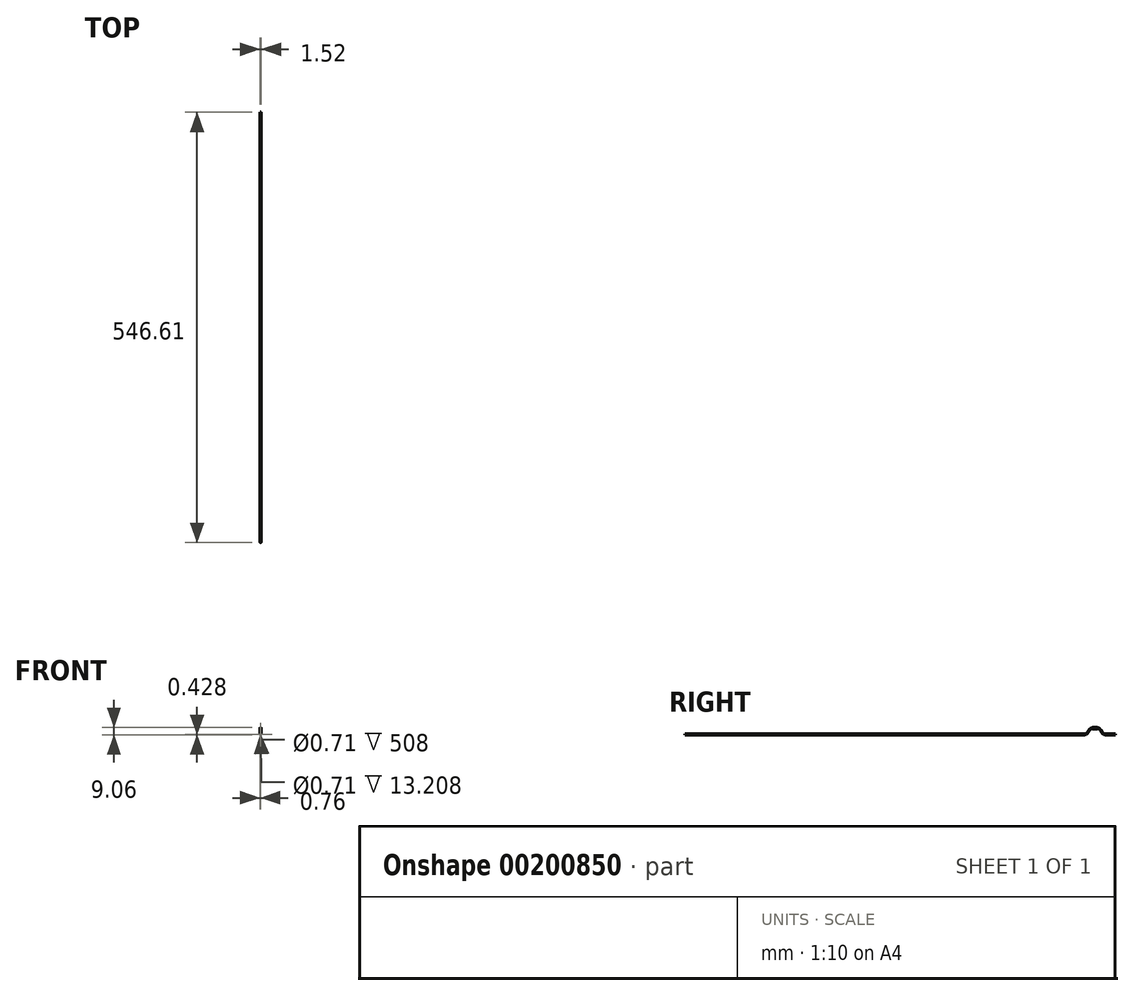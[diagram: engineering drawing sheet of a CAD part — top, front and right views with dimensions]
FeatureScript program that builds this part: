
annotation { "Feature Type Name" : "Feature", "Feature Type Description" : "" }
export const myFeature = defineFeature(function(context is Context, id is Id, definition is map)
    precondition{}
    {
        {
            var Q0;
            Q0=qCreatedBy(makeId("Right.planeOp"),FACE);
            var sketch = newSketch(context, id + "F0", { "sketchPlane" : qUnion([Q0])});
            skLineSegment(sketch, "E0", {"start": v(0, 0) * mm, "end": v(-13.2, 0) * mm});
            skFitSpline(sketch, "E1", {"points": [v(-13.2, 0) * mm, v(-16.07, 1.9) * mm, v(-18.85, 6) * mm, v(-22.86, 7.87) * mm], "startDerivative": vector(-13.47, 0) * mm, "endDerivative": vector(-16.64, 0) * mm});
            skLineSegment(sketch, "E2", {"start": v(-22.86, 7.87) * mm, "end": v(-28.96, 7.87) * mm});
            skLineSegment(sketch, "E3", {"start": v(-25.9, 37.72) * mm, "end": v(-25.9, -23.67) * mm, "construction": true});
            skPoint(sketch, "E4", {"position": v(-25.9, 7.87) * mm});
            skFitSpline(sketch, "E5.MirrorCS", {"points": [v(-38.6, 0) * mm, v(-35.74, 1.9) * mm, v(-32.96, 6) * mm, v(-28.96, 7.87) * mm], "startDerivative": vector(13.47, 0) * mm, "endDerivative": vector(16.64, 0) * mm});
            skLineSegment(sketch, "E6", {"start": v(-38.6, 0) * mm, "end": v(-546.6, 0) * mm});
            skSolve(sketch);
        }
        {
            var Q0;
            Q0=qCreatedBy(makeId("Front.planeOp"),FACE);
            var sketch = newSketch(context, id + "F1", { "sketchPlane" : qUnion([Q0])});
            skCircle(sketch, "E7", {"center": v(0, -0.43) * mm, "radius": 0.43 * mm});
            skCircle(sketch, "E8", {"center": v(0, -0.43) * mm, "radius": 0.36 * mm});
            skSolve(sketch);
        }
        {
            var Q0;
            Q0 = qSketchRegion(id + "F1", true);
            var Q1;
            Q1 = qConstructionFilter(qBodyType(qCreatedBy(id + "F0" ,EDGE), BodyType.WIRE), ConstructionObject.NO);
            sweep(context, id + "F2", {"profiles" : qUnion([Q0]), "path" : qUnion([Q1])});
        }
        {
            var Q0;
            Q0=qCreatedBy(makeId("Front.planeOp"),FACE);
            cPlane(context, id + "F3", {"entities" : qUnion([Q0]), "cplaneType" : CPlaneType.OFFSET, "offset" : 22.86 * mm, "width" : 152.4 * mm, "height" : 152.4 * mm});
        }
        {
            var Q0;
            Q0=qCreatedBy(id+"F3.planeOp",FACE);
            var sketch = newSketch(context, id + "F4", { "sketchPlane" : qUnion([Q0])});
            skCircle(sketch, "E9.0", {"center": v(0, 7.44) * mm, "radius": 0.43 * mm, "construction": true});
            skCircle(sketch, "E10", {"center": v(0, 7.44) * mm, "radius": 0.76 * mm});
            skSolve(sketch);
        }
        {
            var Q0;
            Q0 = qSketchRegion(id + "F4", true);
            extrude(context, id + "F5", {"entities" : qUnion([Q0]), "operationType" : NewBodyOperationType.ADD, "depth" : 6.1 * mm});
        }
    });
